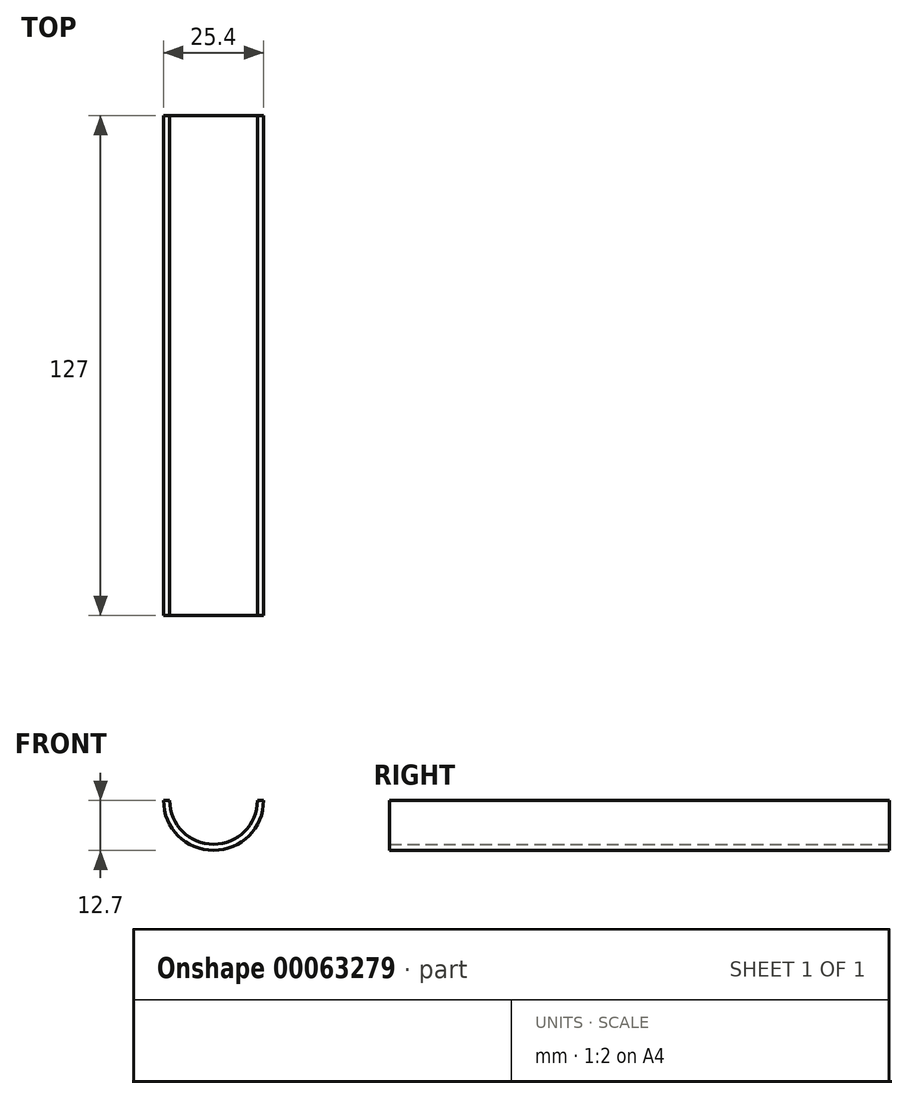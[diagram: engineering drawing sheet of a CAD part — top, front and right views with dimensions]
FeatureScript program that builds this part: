
annotation { "Feature Type Name" : "Feature", "Feature Type Description" : "" }
export const myFeature = defineFeature(function(context is Context, id is Id, definition is map)
    precondition{}
    {
        {
            var Q0;
            Q0=qCreatedBy(makeId("Front.planeOp"),FACE);
            var sketch = newSketch(context, id + "F0", { "sketchPlane" : qUnion([Q0])});
            skArc(sketch, "E0", {"start": v(-12.7, 0) * mm, "mid": v(0, -12.7) * mm, "end": v(12.7, 0) * mm});
            skLineSegment(sketch, "E1", {"start": v(-12.7, 0) * mm, "end": v(12.7, 0) * mm});
            skSolve(sketch);
        }
        {
            var Q0;
            Q0 = qSketchRegion(id + "F0", true);
            extrude(context, id + "F1", {"entities" : qUnion([Q0]), "depth" : 127 * mm});
        }
        {
            var Q0;
            Q0=qCreatedBy(makeId("Front.planeOp"),FACE);
            var sketch = newSketch(context, id + "F2", { "sketchPlane" : qUnion([Q0])});
            skCircle(sketch, "E2", {"center": v(0, 0) * mm, "radius": 11.11 * mm});
            skSolve(sketch);
        }
        {
            var Q0;
            Q0 = qSketchRegion(id + "F2", true);
            extrude(context, id + "F3", {"entities" : qUnion([Q0]), "operationType" : NewBodyOperationType.ADD, "depth" : 127 * mm});
        }
        {
            var Q0;
            Q0=makeQuery(id+"F3.boolean.opBoolean","MERGE",FACE,{"derivedFrom":[makeQuery(id+"F1.opExtrude","CAP_FACE",FACE,{"disambiguationData":[OSD([sQuery(id+"F0.wireOp",EDGE,"E0"),sQuery(id+"F0.wireOp",EDGE,"E1")])],"isStart":true}),makeQuery(id+"F3.opExtrude","CAP_FACE",FACE,{"disambiguationData":[OSD([sQuery(id+"F2.wireOp",EDGE,"E2")])],"isStart":true})]});
            var sketch = newSketch(context, id + "F4", { "sketchPlane" : qUnion([Q0])});
            skCircle(sketch, "E3", {"center": v(0, 0) * mm, "radius": 11.13 * mm});
            skSolve(sketch);
        }
        {
            var Q0;
            Q0 = qSketchRegion(id + "F4", true);
            extrude(context, id + "F5", {"entities" : qUnion([Q0]), "operationType" : NewBodyOperationType.REMOVE, "oppositeDirection" : true, "depth" : 409.9 * mm});
        }
    });
